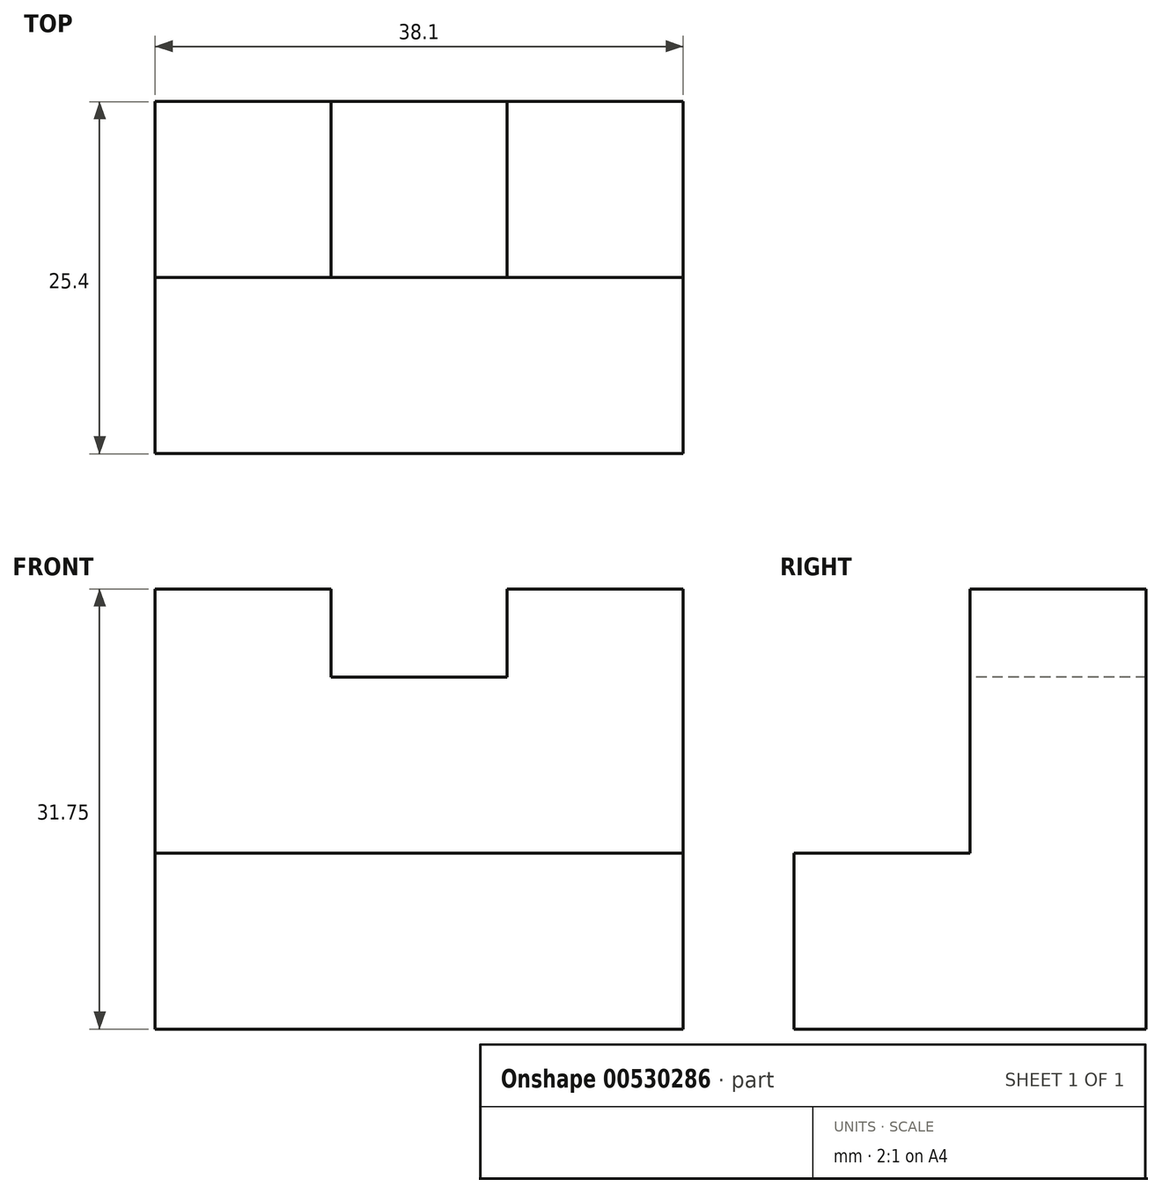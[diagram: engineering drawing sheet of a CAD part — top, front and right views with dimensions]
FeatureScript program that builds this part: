
annotation { "Feature Type Name" : "Feature", "Feature Type Description" : "" }
export const myFeature = defineFeature(function(context is Context, id is Id, definition is map)
    precondition{}
    {
        {
            var Q0;
            Q0=qCreatedBy(makeId("Right.planeOp"),FACE);
            var sketch = newSketch(context, id + "F0", { "sketchPlane" : qUnion([Q0])});
            skLineSegment(sketch, "E0", {"start": v(-23.05, 31.75) * mm, "end": v(-23.05, 0) * mm});
            skLineSegment(sketch, "E1", {"start": v(-23.05, 0) * mm, "end": v(-48.45, 0) * mm});
            skLineSegment(sketch, "E2", {"start": v(-48.45, 0) * mm, "end": v(-48.45, 12.7) * mm});
            skLineSegment(sketch, "E3", {"start": v(-48.45, 12.7) * mm, "end": v(-35.75, 12.7) * mm});
            skLineSegment(sketch, "E4", {"start": v(-35.75, 12.7) * mm, "end": v(-35.75, 31.75) * mm});
            skLineSegment(sketch, "E5", {"start": v(-35.75, 31.75) * mm, "end": v(-23.05, 31.75) * mm});
            skSolve(sketch);
        }
        {
            var Q0;
            Q0 = qSketchRegion(id + "F0", true);
            var Q1;
            Q1 = qSketchRegion(id + "F9ZTBFKCEXpEqlo_1", true);
            extrude(context, id + "F1", {"entities" : qUnion([Q0, Q1]), "depth" : 38.1 * mm, "offsetDistance" : 25.4 * mm});
        }
        {
            var Q0;
            Q0=makeQuery(id+"F1.opExtrude","SWEPT_FACE",FACE,{"disambiguationData":[OSD([sQuery(id+"F0.wireOp",EDGE,"E4")])]});
            var sketch = newSketch(context, id + "F2", { "sketchPlane" : qUnion([Q0])});
            skLineSegment(sketch, "E6", {"start": v(12.7, 31.75) * mm, "end": v(12.7, 25.4) * mm});
            skLineSegment(sketch, "E7", {"start": v(12.7, 25.4) * mm, "end": v(25.4, 25.4) * mm});
            skLineSegment(sketch, "E8", {"start": v(25.4, 25.4) * mm, "end": v(25.4, 31.75) * mm});
            skSolve(sketch);
        }
        {
            var Q0;
            {var subQ0=sQuery(id+"F2.wireOp",EDGE,"E6");Q0=makeQuery(id+"F2.imprint","IMPRINT",FACE,{"disambiguationData":[TD([[makeQuery(id+"F2.imprint","IMPRINT",EDGE,{"derivedFrom":subQ0}),1.0]])]});}
            extrude(context, id + "F3", {"entities" : qUnion([Q0]), "operationType" : NewBodyOperationType.REMOVE, "oppositeDirection" : true, "depth" : 12.7 * mm, "offsetDistance" : 25.4 * mm});
        }
    });
